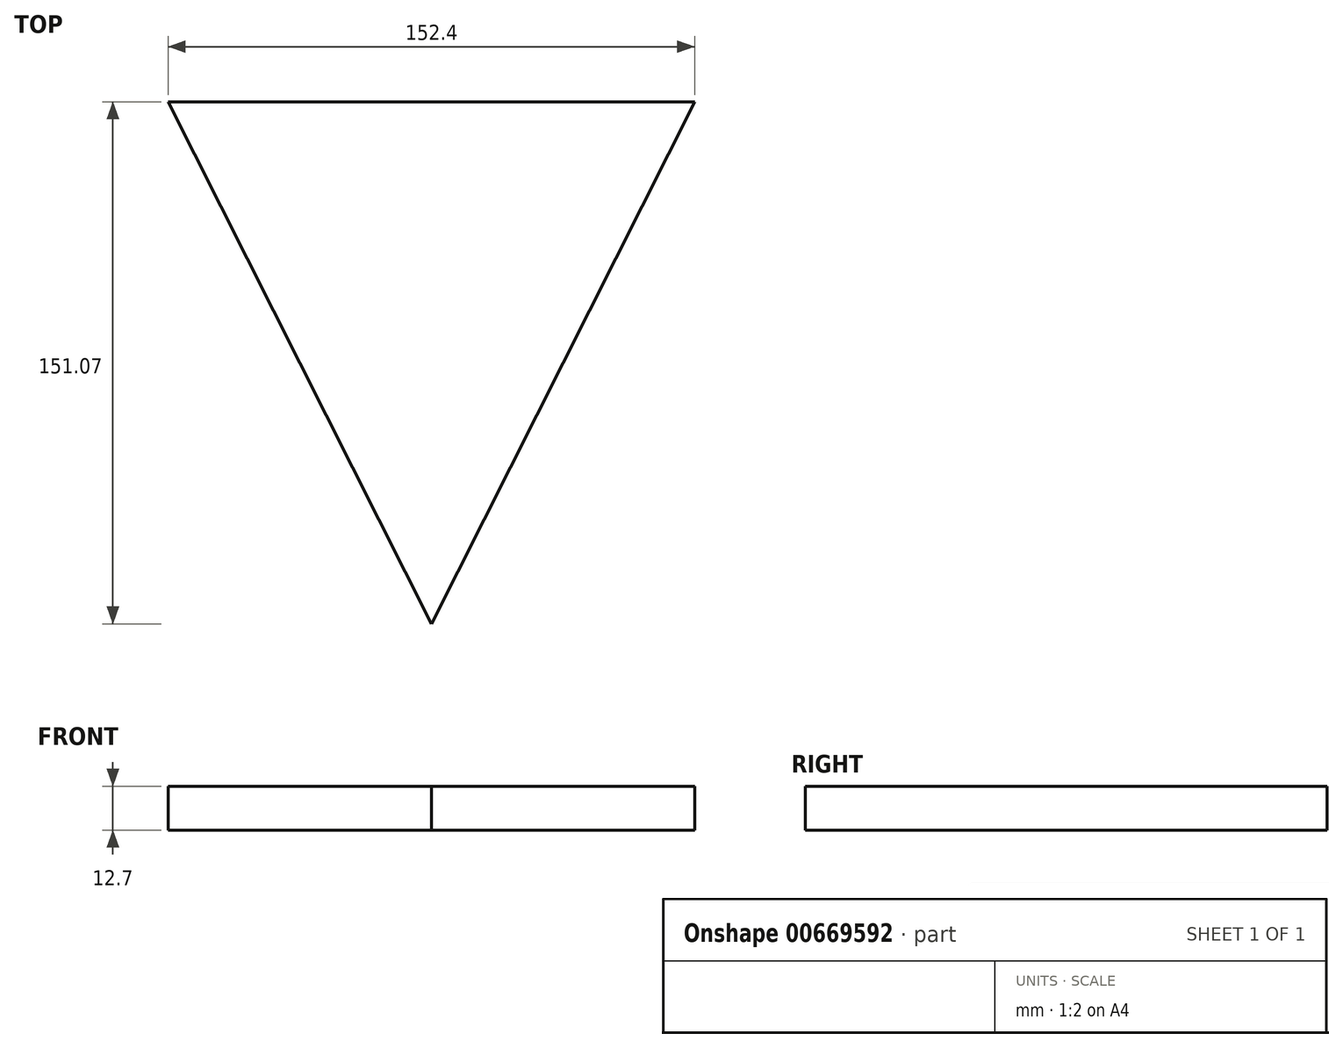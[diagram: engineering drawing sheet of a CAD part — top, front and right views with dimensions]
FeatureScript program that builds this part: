
annotation { "Feature Type Name" : "Feature", "Feature Type Description" : "" }
export const myFeature = defineFeature(function(context is Context, id is Id, definition is map)
    precondition{}
    {
        {
            var Q0;
            Q0=qCreatedBy(makeId("Top.planeOp"),FACE);
            var sketch = newSketch(context, id + "F0", { "sketchPlane" : qUnion([Q0])});
            skLineSegment(sketch, "E0", {"start": v(-76.2, 76.2) * mm, "end": v(76.2, 76.2) * mm});
            skLineSegment(sketch, "E1", {"start": v(76.2, 76.2) * mm, "end": v(0, -74.87) * mm});
            skLineSegment(sketch, "E2", {"start": v(0, -74.87) * mm, "end": v(-76.2, 76.2) * mm});
            skSolve(sketch);
        }
        {
            var Q0;
            Q0 = qSketchRegion(id + "F0", true);
            extrude(context, id + "F1", {"entities" : qUnion([Q0]), "depth" : 12.7 * mm, "offsetDistance" : 25.4 * mm});
        }
    });
